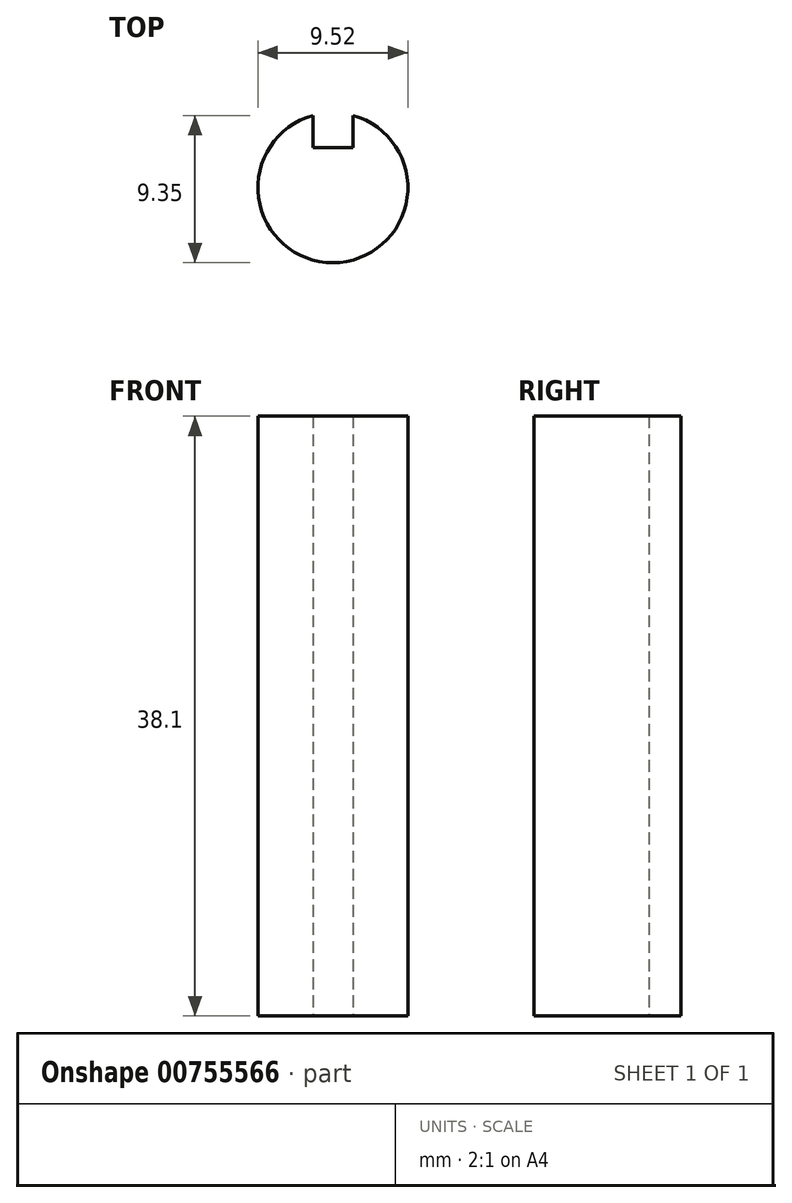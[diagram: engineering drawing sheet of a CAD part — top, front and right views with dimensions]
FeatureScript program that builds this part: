
annotation { "Feature Type Name" : "Feature", "Feature Type Description" : "" }
export const myFeature = defineFeature(function(context is Context, id is Id, definition is map)
    precondition{}
    {
        {
            var Q0;
            Q0=qCreatedBy(makeId("Top.planeOp"),FACE);
            var sketch = newSketch(context, id + "F0", { "sketchPlane" : qUnion([Q0])});
            skArc(sketch, "E0", {"start": v(-1.27, 4.6) * mm, "mid": v(0, -4.76) * mm, "end": v(1.27, 4.6) * mm});
            skLineSegment(sketch, "E1.top", {"start": v(-1.27, 2.54) * mm, "end": v(1.27, 2.54) * mm});
            skLineSegment(sketch, "E1.left", {"start": v(-1.27, 4.6) * mm, "end": v(-1.27, 2.54) * mm});
            skLineSegment(sketch, "E1.right", {"start": v(1.27, 4.6) * mm, "end": v(1.27, 2.54) * mm});
            skSolve(sketch);
        }
        {
            var Q0;
            Q0 = qSketchRegion(id + "F0", true);
            extrude(context, id + "F1", {"entities" : qUnion([Q0]), "depth" : 38.1 * mm, "offsetDistance" : 25.4 * mm});
        }
    });
